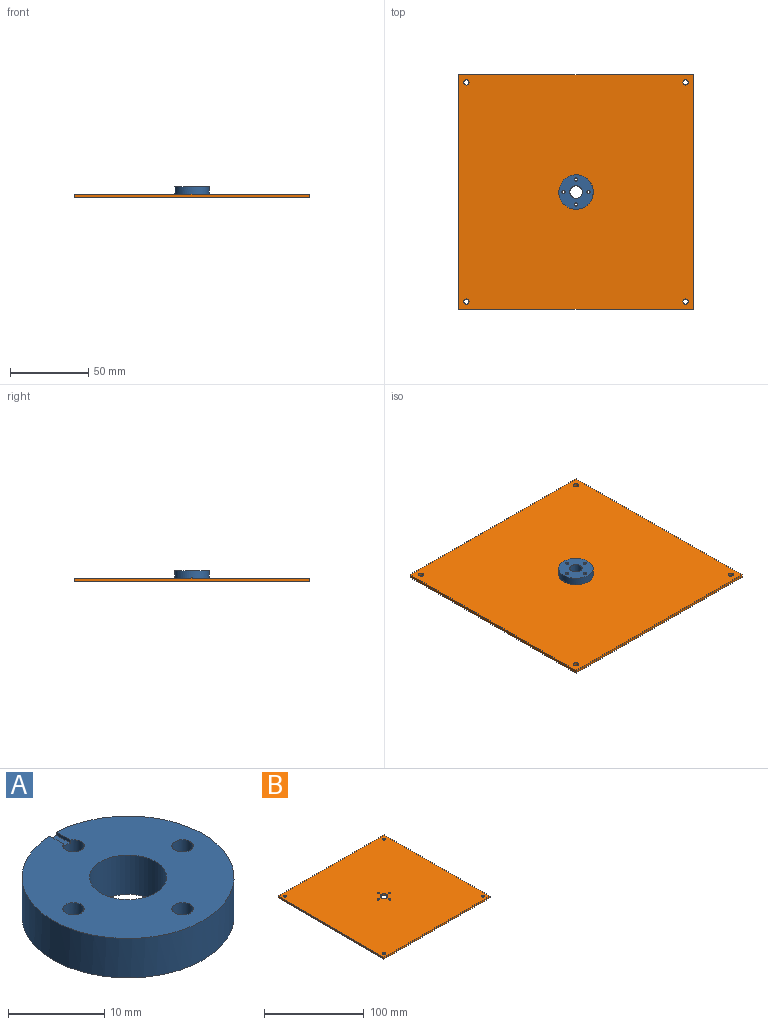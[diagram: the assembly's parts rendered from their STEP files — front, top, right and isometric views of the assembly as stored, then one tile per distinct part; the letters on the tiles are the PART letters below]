
ASSEMBLY  parts=2 mates=1
PART A: 11 faces, bbox 22x22x5 mm
  f0: plane 22x21.99mm, normal (0,0,1), area 312.7mm2, adj f1,f2,f3,f5,f6,f7,f8,f9
  f1: cylinder r=1.1mm len=5mm, axis (0,0,-1), area 34.1mm2, adj f0,f4,f8,f9,f10
  f2: cylinder r=4mm len=8mm, axis (0,0,-1), area 125.7mm2, adj f0,f4
  f3: cylinder r=11mm len=22mm, axis (0,0,-1), area 345.2mm2, adj f0,f4,f8,f9,f10
  f4: plane 22x22mm, normal (0,0,-1), area 314.7mm2, adj f1,f2,f3,f5,f6,f7
  f5: cylinder r=1.1mm len=5mm, axis (0,0,-1), area 34.6mm2, adj f0,f4
  f6: cylinder r=1.1mm len=5mm, axis (0,0,-1), area 34.6mm2, adj f0,f4
  f7: cylinder r=1.1mm len=5mm, axis (0,0,-1), area 34.6mm2, adj f0,f4
  f8: plane 2.01x0.4mm, normal (-1,0,0), area 0.8mm2, adj f0,f1,f3,f10
  f9: plane 2.01x0.4mm, normal (1,0,0), area 0.8mm2, adj f0,f1,f3,f10
  f10: plane 2.02x1mm, normal (0,0,1), area 1.9mm2, adj f1,f3,f8,f9
PART B: 15 faces, bbox 150x150x2 mm
  f0: plane 150x2mm, normal (-1,0,0), area 300mm2, adj f1,f4,f5,f6
  f1: plane 150x2mm, normal (0,-1,0), area 300mm2, adj f0,f2,f5,f6
  f2: plane 150x2mm, normal (1,0,0), area 300mm2, adj f1,f4,f5,f6
  f3: cylinder r=4mm len=8mm, axis (0,0,-1), area 50.3mm2, adj f5,f6
  f4: plane 150x2mm, normal (0,1,0), area 300mm2, adj f0,f2,f5,f6
  f5: plane 150x150mm, normal (0,0,1), area 22400.3mm2, adj f0,f1,f2,f3,f4,f7,f8,f9
  f6: plane 150x150mm, normal (0,0,-1), area 22400.3mm2, adj f0,f1,f2,f3,f4,f7,f8,f9
  f7: cylinder r=1.1mm len=2.2mm, axis (0,0,-1), area 13.8mm2, adj f5,f6
  f8: cylinder r=1.1mm len=2.2mm, axis (0,0,-1), area 13.8mm2, adj f5,f6
  f9: cylinder r=1.1mm len=2.2mm, axis (0,0,-1), area 13.8mm2, adj f5,f6
  f10: cylinder r=1.1mm len=2.2mm, axis (0,0,-1), area 13.8mm2, adj f5,f6
  f11: cylinder r=1.65mm len=3.3mm, axis (0,0,-1), area 20.7mm2, adj f5,f6
  f12: cylinder r=1.65mm len=3.3mm, axis (0,0,-1), area 20.7mm2, adj f5,f6
  f13: cylinder r=1.65mm len=3.3mm, axis (0,0,-1), area 20.7mm2, adj f5,f6
  f14: cylinder r=1.65mm len=3.3mm, axis (0,0,-1), area 20.7mm2, adj f5,f6
PLACE A rot(axis=(-0.71,0.71,0),180deg) t=(117.35,38.42,-1.3)mm
PLACE B t=(117.35,38.42,-8.3)mm
MATE fastened A.f1 <-> B.f8  axis (0,0,-1) through (109.35,38.42,-6.3)mm
